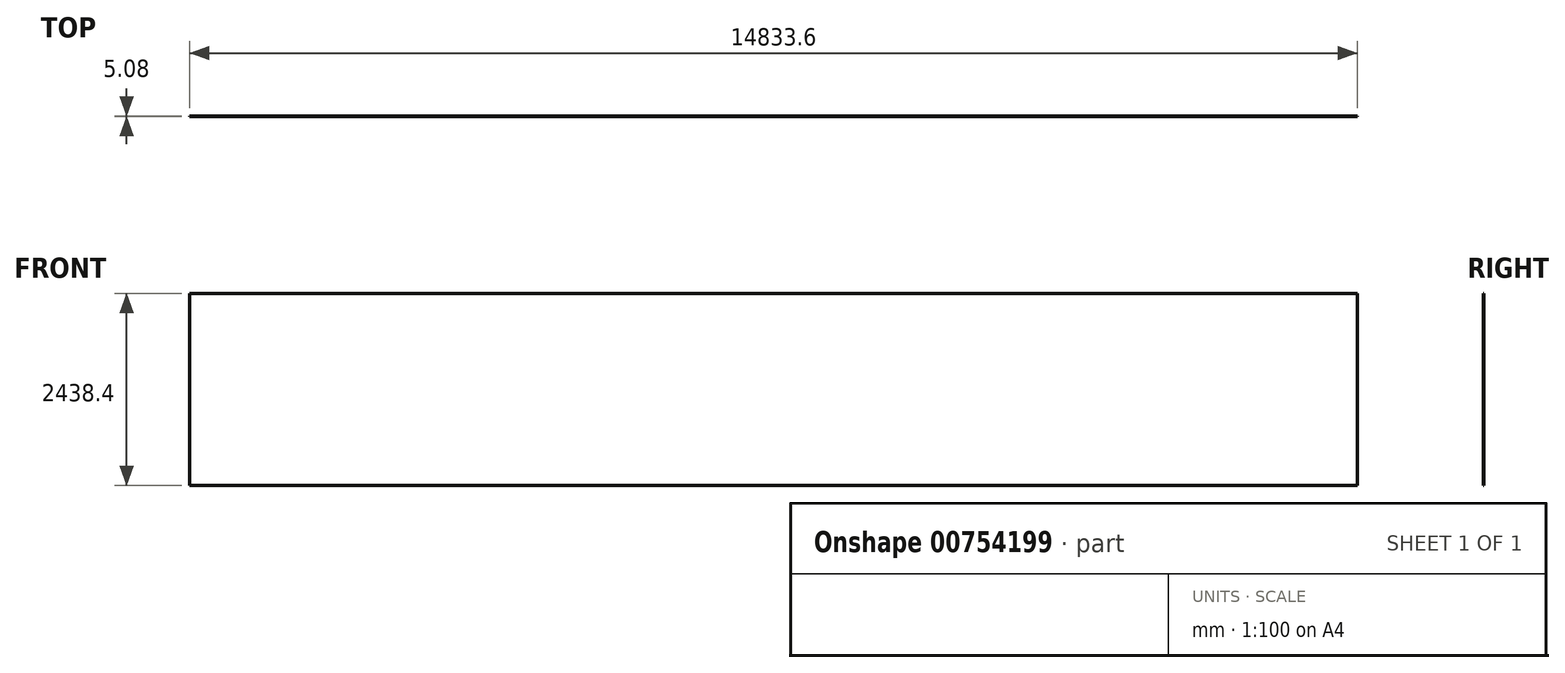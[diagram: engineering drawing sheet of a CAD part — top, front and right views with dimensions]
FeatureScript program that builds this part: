
annotation { "Feature Type Name" : "Feature", "Feature Type Description" : "" }
export const myFeature = defineFeature(function(context is Context, id is Id, definition is map)
    precondition{}
    {
        {
            var Q0;
            Q0=qCreatedBy(makeId("Front.planeOp"),FACE);
            var sketch = newSketch(context, id + "F0", { "sketchPlane" : qUnion([Q0])});
            skLineSegment(sketch, "E0.bottom", {"start": v(-7416.8, 1219.2) * mm, "end": v(7416.8, 1219.2) * mm});
            skLineSegment(sketch, "E0.top", {"start": v(-7416.8, -1219.2) * mm, "end": v(7416.8, -1219.2) * mm});
            skLineSegment(sketch, "E0.left", {"start": v(-7416.8, 1219.2) * mm, "end": v(-7416.8, -1219.2) * mm});
            skLineSegment(sketch, "E0.right", {"start": v(7416.8, 1219.2) * mm, "end": v(7416.8, -1219.2) * mm});
            skPoint(sketch, "E0.middle", {"position": v(0, 0) * mm});
            skSolve(sketch);
        }
        {
            var Q0;
            Q0=makeQuery(id+"F0.imprint","IMPRINT",FACE,{"disambiguationData":[TD([[makeQuery(id+"F0.imprint","IMPRINT",EDGE,{"derivedFrom":sQuery(id+"F0.wireOp",EDGE,"E0.bottom")}),-1.0]])]});
            extrude(context, id + "F1", {"entities" : qUnion([Q0]), "depth" : 5.08 * mm, "offsetDistance" : 25.4 * mm});
        }
    });
